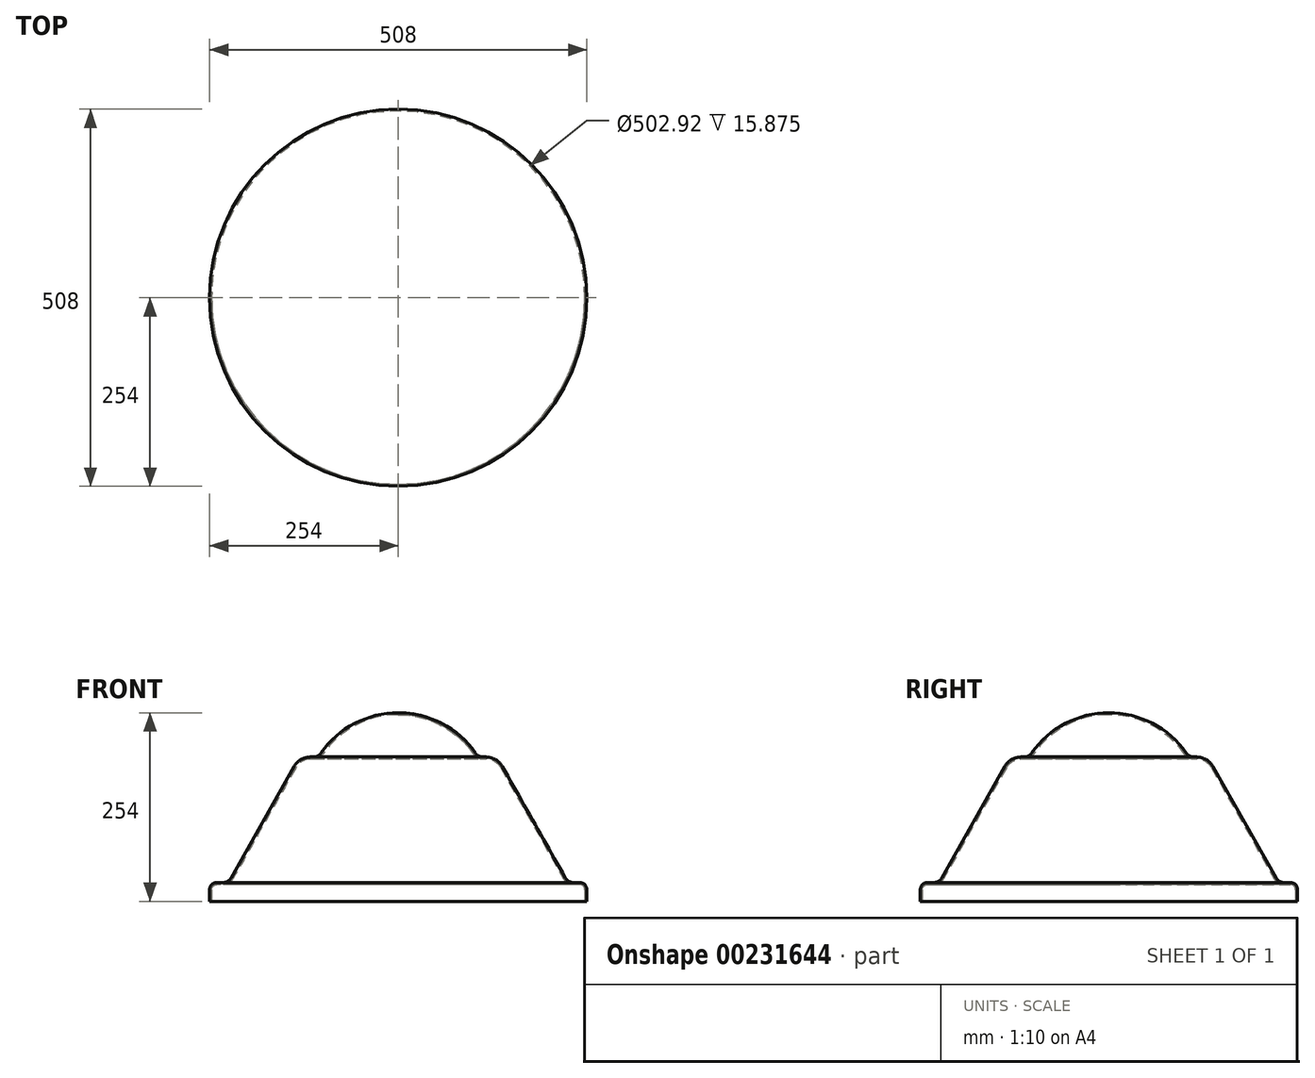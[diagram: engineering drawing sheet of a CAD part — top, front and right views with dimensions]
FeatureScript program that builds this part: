
annotation { "Feature Type Name" : "Feature", "Feature Type Description" : "" }
export const myFeature = defineFeature(function(context is Context, id is Id, definition is map)
    precondition{}
    {
        {
            var Q0;
            Q0=qCreatedBy(makeId("Front.planeOp"),FACE);
            var sketch = newSketch(context, id + "F0", { "sketchPlane" : qUnion([Q0])});
            skLineSegment(sketch, "E0", {"start": v(0, 0) * mm, "end": v(254, 0) * mm});
            skLineSegment(sketch, "E1", {"start": v(254, 0) * mm, "end": v(254, 25.4) * mm});
            skLineSegment(sketch, "E2", {"start": v(254, 25.4) * mm, "end": v(228.6, 25.4) * mm});
            skArc(sketch, "E3", {"start": v(107.61, 194.44) * mm, "mid": v(61.5, 238.12) * mm, "end": v(0, 254) * mm});
            skLineSegment(sketch, "E4", {"start": v(107.61, 194.44) * mm, "end": v(133.01, 194.44) * mm});
            skLineSegment(sketch, "E5", {"start": v(133.01, 194.44) * mm, "end": v(228.6, 25.4) * mm});
            skLineSegment(sketch, "E6", {"start": v(0, 0) * mm, "end": v(0, 254) * mm});
            skSolve(sketch);
        }
        {
            var Q0;
            Q0 = qSketchRegion(id + "F0", true);
            var Q1;
            Q1=sQuery(id+"F0.wireOp",EDGE,"E6");
            revolve(context, id + "F1", {"entities" : qUnion([Q0]), "axis" : qUnion([Q1]), "revolveType" : RevolveType.FULL});
        }
        {
            var Q0;
            Q0=makeQuery(id+"F1.opRevolve","SWEPT_EDGE",EDGE,{"disambiguationData":[OSD([sQuery(id+"F0.wireOp",EDGE,"E2"),sQuery(id+"F0.wireOp",EDGE,"E5")])]});
            fillet(context, id + "F2", {"entities" : qUnion([Q0]), "radius" : 12.7 * mm, "tangentPropagation" : true, "allowEdgeOverflow" : false});
        }
        {
            var Q0;
            Q0=makeQuery(id+"F1.opRevolve","SWEPT_EDGE",EDGE,{"disambiguationData":[OSD([sQuery(id+"F0.wireOp",EDGE,"E1"),sQuery(id+"F0.wireOp",EDGE,"E2")])]});
            fillet(context, id + "F3", {"entities" : qUnion([Q0]), "radius" : 9.52 * mm, "tangentPropagation" : true, "allowEdgeOverflow" : false});
        }
        {
            var Q0;
            Q0=makeQuery(id+"F1.opRevolve","SWEPT_EDGE",EDGE,{"disambiguationData":[OSD([sQuery(id+"F0.wireOp",EDGE,"E4"),sQuery(id+"F0.wireOp",EDGE,"E5")])]});
            fillet(context, id + "F4", {"entities" : qUnion([Q0]), "radius" : 25.4 * mm, "tangentPropagation" : true, "allowEdgeOverflow" : false});
        }
        {
            var Q0;
            Q0=makeQuery(id+"F1.opRevolve","SWEPT_EDGE",EDGE,{"disambiguationData":[OSD([sQuery(id+"F0.wireOp",EDGE,"E3"),sQuery(id+"F0.wireOp",EDGE,"E4")])]});
            fillet(context, id + "F5", {"entities" : qUnion([Q0]), "radius" : 12.7 * mm, "tangentPropagation" : true, "allowEdgeOverflow" : false});
        }
        {
            var Q0;
            Q0=makeQuery(id+"F1.opRevolve","SWEPT_FACE",FACE,{"disambiguationData":[OSD([sQuery(id+"F0.wireOp",EDGE,"E0")])]});
            shell(context, id + "F6", {"entities" : qUnion([Q0]), "thickness" : 2.54 * mm});
        }
    });
